# Revit family: KSL_Kemlu-Sanchion [0deg] Mount
name_source: partatom
category: Lighting Fixtures
units: mm (PartAtom-declared; Revit-internal decimal feet)

## family parameters
Cut with Voids When Loaded = No
Host = Face
Light Source = Yes
OmniClass Number = 23.80.70.14
OmniClass Title = Luminaries for External Lighting
Part Type = Normal
Room Calculation Point = No
Round Connector Dimension = Use Diameter
Shared = No

## types (9) — shared parameters
Color Filter = 16777215
Default Elevation = 4' - 0"
Description = Enclosed and gasketed LED fixture series
Dimming Lamp Color Temperature Shift = <None>
Emit Shape Visible in Rendering = No
Emit from Circle Diameter = 0' - 11"
Glass = White Glass
Load Classification = Lighting
Manufacturer = Columbia Lighting
Material Finish = Powdercoat - Gray
Model = KSL - Kemlux III LED Series
Mount = Stanchion 0˚
Power Factor = 1
Tilt Angle = -90.00°
URL = https://www.currentlighting.com
Voltage = 277 V

## per-type parameters (varying)
| type | Apparent Load | Lamp | Optics | Photometric Web File | Watt | Wattage Comments |
| KSL-18L-X-5K-5M | 43 VA | 18 High Performanc LEDs | Type V Square | KXL-18L-X-5K-5M.ies | 43 W | 43 Watts |
| KSL-18L-X-5K-5R | 43 VA | 18 High Performanc LEDs | Type V Rectangle | KXL-18L-X-5K-5R.ies | 43 W | 43 Watts |
| KSL-18L-X-5K-N | 43 VA | 18 High Performanc LEDs | Narrow | KXL-18L-X-5K-N.ies | 43 W | 43 Watts |
| KSL-24L-X-5K-5M | 57 VA | 24 High Performanc LEDs | Type V Square | KXL-24L-X-5K-5M.ies | 57 W | 57 Watts |
| KSL-24L-X-5K-5R | 57 VA | 24 High Performanc LEDs | Type V Rectangle | KXL-24L-X-5K-5R.ies | 57 W | 57 Watts |
| KSL-24L-X-5K-N | 57 VA | 24 High Performanc LEDs | Narrow | KXL-24L-X-5K-N.ies | 57 W | 57 Watts |
| KSL-36L-X-5K-5M | 86 VA | 36 High Performanc LEDs | Type V Square | KXL-36L-X-5K-5M.ies | 86 W | 86 Watts |
| KSL-36L-X-5K-5R | 86 VA | 36 High Performanc LEDs | Type V Rectangle | KXL-36L-X-5K-5R.ies | 86 W | 86 Watts |
| KSL-36L-X-5K-N | 86 VA | 36 High Performanc LEDs | Narrow | KXL-36L-X-5K-N.ies | 86 W | 86 Watts |

## geometry (parser evidence)
native form markers: Blend x8, Sweep x2
no freeform markers — native parametric forms only
